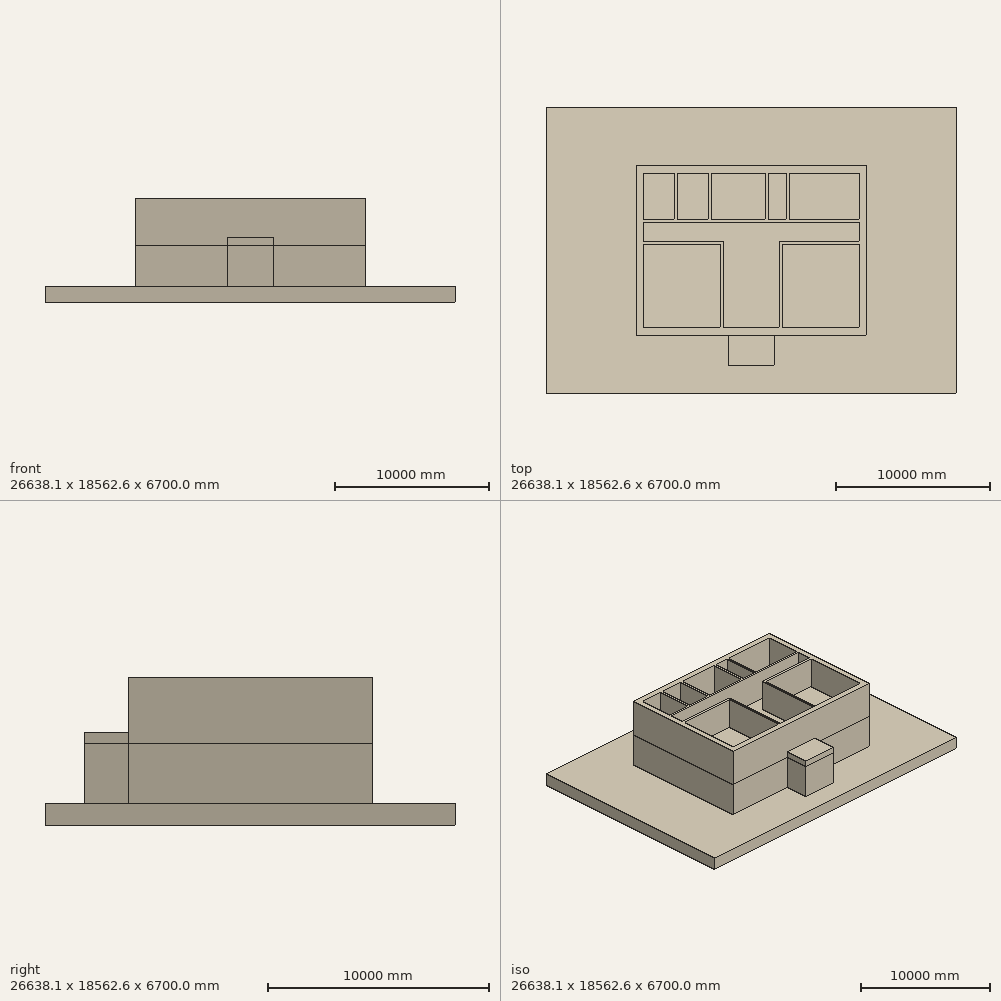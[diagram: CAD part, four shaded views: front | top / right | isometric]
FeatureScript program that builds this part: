
annotation { "Feature Type Name" : "Feature", "Feature Type Description" : "" }
export const myFeature = defineFeature(function(context is Context, id is Id, definition is map)
    precondition{}
    {
        {
            var Q0;
            Q0=qCreatedBy(makeId("Top.planeOp"),FACE);
            var sketch = newSketch(context, id + "F0", { "sketchPlane" : qUnion([Q0])});
            skLineSegment(sketch, "E0.bottom", {"start": v(-7500, -5500) * mm, "end": v(-1500, -5500) * mm});
            skLineSegment(sketch, "E0.top", {"start": v(-7500, 5500) * mm, "end": v(7500, 5500) * mm});
            skLineSegment(sketch, "E0.left", {"start": v(-7500, -5500) * mm, "end": v(-7500, 5500) * mm});
            skLineSegment(sketch, "E0.right", {"start": v(7500, -5500) * mm, "end": v(7500, 5500) * mm});
            skPoint(sketch, "E0.middle", {"position": v(0, 0) * mm});
            skLineSegment(sketch, "E1.bottom", {"start": v(-7000, -5000) * mm, "end": v(-1500, -5000) * mm});
            skLineSegment(sketch, "E1.top", {"start": v(-7000, 5000) * mm, "end": v(-1500, 5000) * mm});
            skLineSegment(sketch, "E1.left", {"start": v(-7000, -5000) * mm, "end": v(-7000, -1500) * mm});
            skLineSegment(sketch, "E1.right", {"start": v(7000, -5000) * mm, "end": v(7000, -4000) * mm});
            skLineSegment(sketch, "E2.top", {"start": v(-1500, -7500) * mm, "end": v(1500, -7500) * mm});
            skLineSegment(sketch, "E2.left", {"start": v(-1500, -5500) * mm, "end": v(-1500, -7500) * mm});
            skLineSegment(sketch, "E2.right", {"start": v(1500, -5500) * mm, "end": v(1500, -7500) * mm});
            skLineSegment(sketch, "E3.trimOffspring", {"start": v(1500, -5500) * mm, "end": v(7500, -5500) * mm});
            skLineSegment(sketch, "E4", {"start": v(-5200, -5000) * mm, "end": v(-5200, -1500) * mm});
            skLineSegment(sketch, "E5", {"start": v(-5200, -1500) * mm, "end": v(-7000, -1500) * mm});
            skLineSegment(sketch, "E6", {"start": v(-7000, -1300) * mm, "end": v(-5000, -1300) * mm});
            skLineSegment(sketch, "E7", {"start": v(-5000, -1500) * mm, "end": v(-5000, -5000) * mm});
            skLineSegment(sketch, "E8", {"start": v(-1300, -5000) * mm, "end": v(-1300, -3150) * mm});
            skLineSegment(sketch, "E9", {"start": v(-1500, -1300) * mm, "end": v(-5000, -1300) * mm});
            skLineSegment(sketch, "E10", {"start": v(-5000, -1500) * mm, "end": v(-1500, -1500) * mm});
            skLineSegment(sketch, "E11", {"start": v(-1500, -1500) * mm, "end": v(-1500, -5000) * mm});
            skLineSegment(sketch, "E12.trimOffspring", {"start": v(-7000, -1300) * mm, "end": v(-7000, 5000) * mm});
            skLineSegment(sketch, "E13.trimOffspring", {"start": v(-1300, -5000) * mm, "end": v(3200, -5000) * mm});
            skLineSegment(sketch, "E14", {"start": v(-1300, -5500) * mm, "end": v(1300, -5500) * mm});
            skLineSegment(sketch, "E15", {"start": v(-1300, -5500) * mm, "end": v(-1300, -7300) * mm});
            skLineSegment(sketch, "E16", {"start": v(-1300, -7300) * mm, "end": v(1300, -7300) * mm});
            skLineSegment(sketch, "E17", {"start": v(1300, -7300) * mm, "end": v(1300, -5500) * mm});
            skPoint(sketch, "E18.orphan", {"position": v(1300, -5000) * mm});
            skLineSegment(sketch, "E19", {"start": v(-1300, -1300) * mm, "end": v(-1300, 3300) * mm});
            skLineSegment(sketch, "E20", {"start": v(-1500, -1300) * mm, "end": v(-1500, 5000) * mm});
            skLineSegment(sketch, "E21.trimOffspring", {"start": v(-1300, 5000) * mm, "end": v(1300, 5000) * mm});
            skLineSegment(sketch, "E22", {"start": v(-1300, 3500) * mm, "end": v(1300, 3500) * mm});
            skLineSegment(sketch, "E23", {"start": v(1300, 3500) * mm, "end": v(1300, 5000) * mm});
            skLineSegment(sketch, "E24", {"start": v(-1300, 3300) * mm, "end": v(1500, 3300) * mm});
            skLineSegment(sketch, "E25", {"start": v(1500, 3300) * mm, "end": v(1500, 5000) * mm});
            skLineSegment(sketch, "E26.trimOffspring", {"start": v(-1300, 3500) * mm, "end": v(-1300, 5000) * mm});
            skLineSegment(sketch, "E27.trimOffspring", {"start": v(1500, 5000) * mm, "end": v(3200, 5000) * mm});
            skLineSegment(sketch, "E28", {"start": v(3200, 5000) * mm, "end": v(3200, -5000) * mm});
            skLineSegment(sketch, "E29", {"start": v(-1300, -3150) * mm, "end": v(1500, -3150) * mm});
            skLineSegment(sketch, "E30", {"start": v(1500, 3300) * mm, "end": v(1500, -3150) * mm});
            skLineSegment(sketch, "E31", {"start": v(1300, 3300) * mm, "end": v(1300, -2950) * mm});
            skLineSegment(sketch, "E32", {"start": v(1300, -2950) * mm, "end": v(-1300, -2950) * mm});
            skLineSegment(sketch, "E33.trimOffspring", {"start": v(-1300, -2950) * mm, "end": v(-1300, -1300) * mm});
            skLineSegment(sketch, "E34", {"start": v(7000, 2500) * mm, "end": v(3400, 2500) * mm});
            skLineSegment(sketch, "E35", {"start": v(3400, 2500) * mm, "end": v(3400, 5000) * mm});
            skLineSegment(sketch, "E36.trimOffspring", {"start": v(3400, 5000) * mm, "end": v(7000, 5000) * mm});
            skPoint(sketch, "E37.orphan", {"position": v(3200, 2500) * mm});
            skLineSegment(sketch, "E38", {"start": v(3400, 2300) * mm, "end": v(3400, -3800) * mm});
            skLineSegment(sketch, "E39", {"start": v(3400, -4000) * mm, "end": v(5000, -4000) * mm});
            skLineSegment(sketch, "E40", {"start": v(5200, -4000) * mm, "end": v(5200, -5000) * mm});
            skLineSegment(sketch, "E41", {"start": v(3400, -3800) * mm, "end": v(7000, -3800) * mm});
            skLineSegment(sketch, "E42", {"start": v(5000, -4000) * mm, "end": v(5000, -5000) * mm});
            skLineSegment(sketch, "E43.trimOffspring", {"start": v(3400, -4000) * mm, "end": v(3400, -5000) * mm});
            skLineSegment(sketch, "E44.trimOffspring", {"start": v(3400, -5000) * mm, "end": v(5000, -5000) * mm});
            skLineSegment(sketch, "E45.trimOffspring", {"start": v(5200, -5000) * mm, "end": v(7000, -5000) * mm});
            skLineSegment(sketch, "E46.trimOffspring", {"start": v(5200, -4000) * mm, "end": v(7000, -4000) * mm});
            skLineSegment(sketch, "E47.trimOffspring", {"start": v(7000, -3800) * mm, "end": v(7000, 2300) * mm});
            skLineSegment(sketch, "E48", {"start": v(3400, 2300) * mm, "end": v(7000, 2300) * mm});
            skLineSegment(sketch, "E49.trimOffspring", {"start": v(7000, 2500) * mm, "end": v(7000, 5000) * mm});
            skSolve(sketch);
        }
        {
            var Q0;
            Q0=qCreatedBy(makeId("Top.planeOp"),FACE);
            var sketch = newSketch(context, id + "F1", { "sketchPlane" : qUnion([Q0])});
            skLineSegment(sketch, "E50.bottom", {"start": v(-102.33, 68.93) * mm, "end": v(33.4, 68.93) * mm});
            skLineSegment(sketch, "E50.top", {"start": v(-102.33, -41.72) * mm, "end": v(33.4, -41.72) * mm});
            skLineSegment(sketch, "E50.left", {"start": v(-102.33, 68.93) * mm, "end": v(-102.33, -41.72) * mm});
            skLineSegment(sketch, "E50.right", {"start": v(33.4, 68.93) * mm, "end": v(33.4, -41.72) * mm});
            skLineSegment(sketch, "E51.bottom", {"start": v(-13319.03, -9281.32) * mm, "end": v(13319.03, -9281.32) * mm});
            skLineSegment(sketch, "E51.top", {"start": v(-13319.03, 9281.32) * mm, "end": v(13319.03, 9281.32) * mm});
            skLineSegment(sketch, "E51.left", {"start": v(-13319.03, -9281.32) * mm, "end": v(-13319.03, 9281.32) * mm});
            skLineSegment(sketch, "E51.right", {"start": v(13319.03, -9281.32) * mm, "end": v(13319.03, 9281.32) * mm});
            skPoint(sketch, "E51.middle", {"position": v(0, 0) * mm});
            skSolve(sketch);
        }
        {
            var Q0;
            Q0 = qSketchRegion(id + "F0", true);
            extrude(context, id + "F2", {"entities" : qUnion([Q0]), "depth" : 2700 * mm, "offsetDistance" : 25 * mm});
        }
        {
            var Q0;
            Q0 = qSketchRegion(id + "F1", true);
            extrude(context, id + "F3", {"entities" : qUnion([Q0]), "operationType" : NewBodyOperationType.ADD, "depth" : -1000 * mm, "offsetDistance" : 25 * mm});
        }
        {
            var Q0;
            Q0=qCreatedBy(makeId("Top.planeOp"),FACE);
            var sketch = newSketch(context, id + "F4", { "sketchPlane" : qUnion([Q0])});
            skLineSegment(sketch, "E52.bottom", {"start": v(-7500, -5500) * mm, "end": v(7500, -5500) * mm});
            skLineSegment(sketch, "E52.top", {"start": v(-7500, 5500) * mm, "end": v(7500, 5500) * mm});
            skLineSegment(sketch, "E52.left", {"start": v(-7500, -5500) * mm, "end": v(-7500, 5500) * mm});
            skLineSegment(sketch, "E52.right", {"start": v(7500, -5500) * mm, "end": v(7500, 5500) * mm});
            skPoint(sketch, "E52.middle", {"position": v(0, 0) * mm});
            skLineSegment(sketch, "E53.bottom", {"start": v(-7000, 5000) * mm, "end": v(-5000, 5000) * mm});
            skLineSegment(sketch, "E53.top", {"start": v(-7000, -5000) * mm, "end": v(-2000, -5000) * mm});
            skLineSegment(sketch, "E53.left", {"start": v(-7000, 5000) * mm, "end": v(-7000, 600) * mm});
            skLineSegment(sketch, "E53.right", {"start": v(7000, 5000) * mm, "end": v(7000, 600) * mm});
            skLineSegment(sketch, "E54.top", {"start": v(-7000, 400) * mm, "end": v(-2000, 400) * mm});
            skLineSegment(sketch, "E54.left", {"start": v(-7000, -5000) * mm, "end": v(-7000, 400) * mm});
            skLineSegment(sketch, "E54.right", {"start": v(-2000, -5000) * mm, "end": v(-2000, 400) * mm});
            skLineSegment(sketch, "E55.bottom", {"start": v(7000, -5000) * mm, "end": v(2000, -5000) * mm});
            skLineSegment(sketch, "E55.top", {"start": v(7000, 400) * mm, "end": v(2000, 400) * mm});
            skLineSegment(sketch, "E55.left", {"start": v(7000, -5000) * mm, "end": v(7000, 400) * mm});
            skLineSegment(sketch, "E55.right", {"start": v(2000, -5000) * mm, "end": v(2000, 400) * mm});
            skLineSegment(sketch, "E56.top", {"start": v(-7000, 2000) * mm, "end": v(-5000, 2000) * mm});
            skLineSegment(sketch, "E56.left", {"start": v(-7000, 5000) * mm, "end": v(-7000, 2000) * mm});
            skLineSegment(sketch, "E56.right", {"start": v(7000, 5000) * mm, "end": v(7000, 2000) * mm});
            skLineSegment(sketch, "E57.top", {"start": v(-7000, 600) * mm, "end": v(-1800, 600) * mm});
            skLineSegment(sketch, "E57.right", {"start": v(-1800, -5000) * mm, "end": v(-1800, 600) * mm});
            skLineSegment(sketch, "E58.top", {"start": v(7000, 600) * mm, "end": v(1800, 600) * mm});
            skLineSegment(sketch, "E58.right", {"start": v(1800, -5000) * mm, "end": v(1800, 600) * mm});
            skLineSegment(sketch, "E59", {"start": v(-2800, 5000) * mm, "end": v(-2800, 2000) * mm});
            skLineSegment(sketch, "E60", {"start": v(1100, 5000) * mm, "end": v(1100, 2000) * mm});
            skLineSegment(sketch, "E61", {"start": v(2300, 5000) * mm, "end": v(2300, 2000) * mm});
            skLineSegment(sketch, "E62", {"start": v(-4800, 2000) * mm, "end": v(-4800, 5000) * mm});
            skLineSegment(sketch, "E63", {"start": v(-2600, 2000) * mm, "end": v(-2600, 5000) * mm});
            skLineSegment(sketch, "E64", {"start": v(2500, 2000) * mm, "end": v(2500, 5000) * mm});
            skLineSegment(sketch, "E65.trimOffspring", {"start": v(-7000, 400) * mm, "end": v(-7000, -5000) * mm});
            skLineSegment(sketch, "E66.trimOffspring", {"start": v(-1800, -5000) * mm, "end": v(1800, -5000) * mm});
            skLineSegment(sketch, "E67.trimOffspring", {"start": v(2000, -5000) * mm, "end": v(7000, -5000) * mm});
            skLineSegment(sketch, "E68.trimOffspring", {"start": v(7000, 400) * mm, "end": v(7000, -5000) * mm});
            skLineSegment(sketch, "E69", {"start": v(900, 5000) * mm, "end": v(900, 2000) * mm});
            skLineSegment(sketch, "E70", {"start": v(-5000, 5000) * mm, "end": v(-5000, 2000) * mm});
            skLineSegment(sketch, "E71.trimOffspring", {"start": v(-4800, 5000) * mm, "end": v(-2800, 5000) * mm});
            skLineSegment(sketch, "E72.trimOffspring", {"start": v(-4800, 2000) * mm, "end": v(-2800, 2000) * mm});
            skLineSegment(sketch, "E73.trimOffspring", {"start": v(-2600, 2000) * mm, "end": v(900, 2000) * mm});
            skLineSegment(sketch, "E74.trimOffspring", {"start": v(-2600, 5000) * mm, "end": v(900, 5000) * mm});
            skLineSegment(sketch, "E75.trimOffspring", {"start": v(2500, 5000) * mm, "end": v(7000, 5000) * mm});
            skLineSegment(sketch, "E76.trimOffspring", {"start": v(1100, 5000) * mm, "end": v(2300, 5000) * mm});
            skLineSegment(sketch, "E77.trimOffspring", {"start": v(1100, 2000) * mm, "end": v(2300, 2000) * mm});
            skLineSegment(sketch, "E78.trimOffspring", {"start": v(2500, 2000) * mm, "end": v(7000, 2000) * mm});
            skLineSegment(sketch, "E79", {"start": v(-7000, 1800) * mm, "end": v(7000, 1800) * mm});
            skSolve(sketch);
        }
        {
            var Q0;
            Q0=qCreatedBy(makeId("Top.planeOp"),FACE);
            var sketch = newSketch(context, id + "F5", { "sketchPlane" : qUnion([Q0])});
            skLineSegment(sketch, "E80.bottom", {"start": v(-7500, -5500) * mm, "end": v(-1500, -5500) * mm});
            skLineSegment(sketch, "E80.top", {"start": v(-7500, 5500) * mm, "end": v(7500, 5500) * mm});
            skLineSegment(sketch, "E80.left", {"start": v(-7500, -5500) * mm, "end": v(-7500, 5500) * mm});
            skLineSegment(sketch, "E80.right", {"start": v(7500, -5500) * mm, "end": v(7500, 5500) * mm});
            skPoint(sketch, "E80.middle", {"position": v(0, 0) * mm});
            skLineSegment(sketch, "E81.top", {"start": v(-1500, -7500) * mm, "end": v(1500, -7500) * mm});
            skLineSegment(sketch, "E81.left", {"start": v(-1500, -5500) * mm, "end": v(-1500, -7500) * mm});
            skLineSegment(sketch, "E81.right", {"start": v(1500, -5500) * mm, "end": v(1500, -7500) * mm});
            skLineSegment(sketch, "E82.trimOffspring", {"start": v(1500, -5500) * mm, "end": v(7500, -5500) * mm});
            skSolve(sketch);
        }
        {
            var Q0;
            Q0=makeQuery(id+"F5.imprint","IMPRINT",FACE,{"disambiguationData":[TD([[makeQuery(id+"F5.imprint","IMPRINT",EDGE,{"derivedFrom":sQuery(id+"F5.wireOp",EDGE,"E80.bottom")}),1.0]])]});
            extrude(context, id + "F6", {"entities" : qUnion([Q0]), "surfaceOperationType" : NewSurfaceOperationType.ADD, "depth" : 3200 * mm, "offsetDistance" : 25 * mm, "hasSecondDirection" : true, "secondDirectionOppositeDirection" : false, "secondDirectionDepth" : 2700 * mm});
        }
        {
            var Q0;
            Q0=makeQuery(id+"F4.imprint","IMPRINT",FACE,{"disambiguationData":[TD([[makeQuery(id+"F4.imprint","IMPRINT",EDGE,{"derivedFrom":sQuery(id+"F4.wireOp",EDGE,"E52.bottom")}),1.0]])]});
            extrude(context, id + "F7", {"entities" : qUnion([Q0]), "operationType" : NewBodyOperationType.ADD, "depth" : 5700 * mm, "offsetDistance" : 25 * mm, "hasSecondDirection" : true, "secondDirectionOppositeDirection" : false, "secondDirectionDepth" : 3200 * mm});
        }
    });
